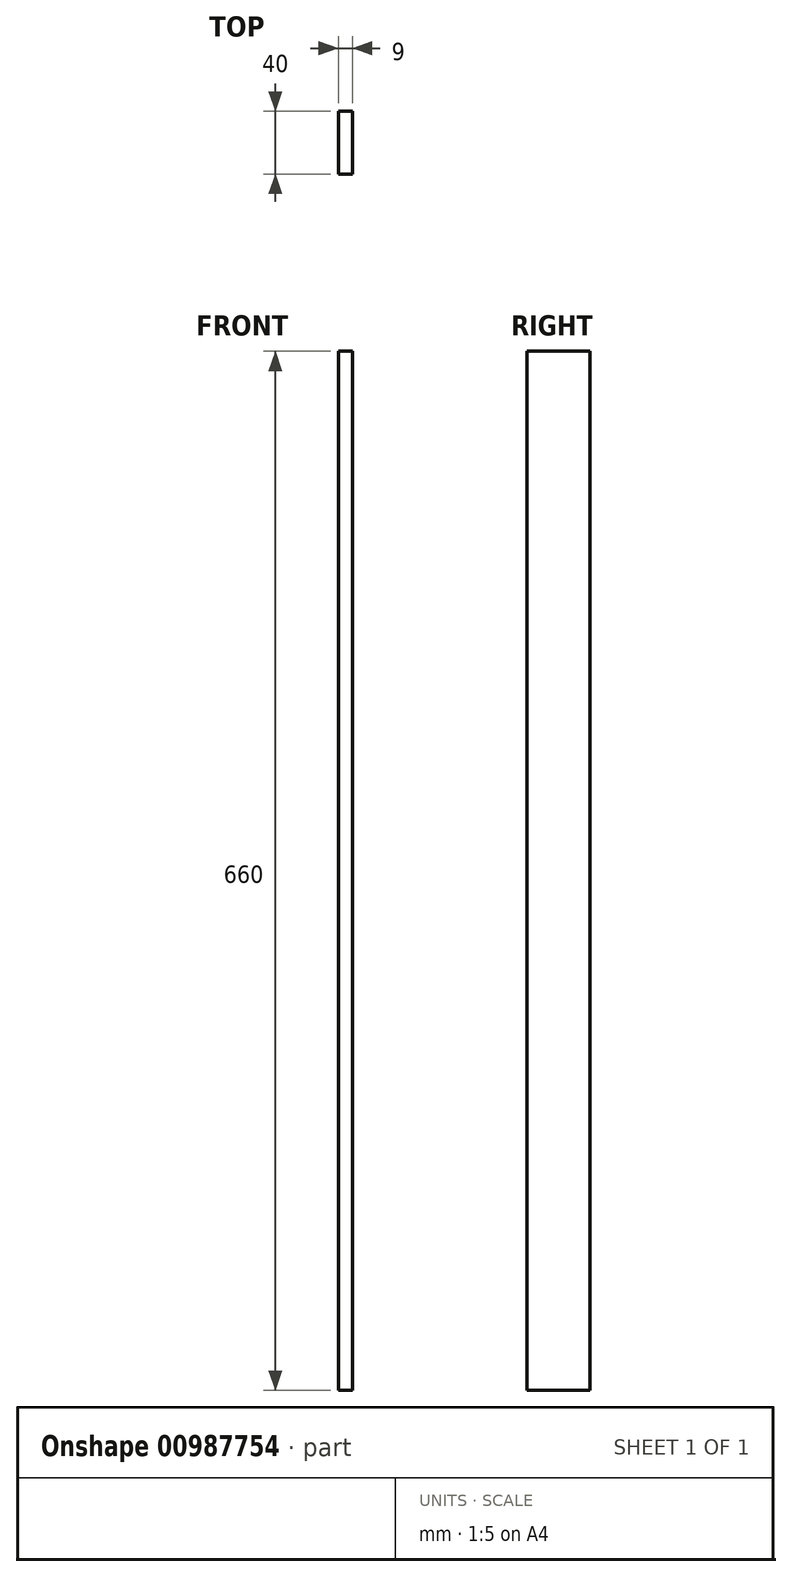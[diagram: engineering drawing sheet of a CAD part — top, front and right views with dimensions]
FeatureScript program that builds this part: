
annotation { "Feature Type Name" : "Feature", "Feature Type Description" : "" }
export const myFeature = defineFeature(function(context is Context, id is Id, definition is map)
    precondition{}
    {
        {
            var Q0;
            Q0=qCreatedBy(makeId("Top.planeOp"),FACE);
            var sketch = newSketch(context, id + "F0", { "sketchPlane" : qUnion([Q0])});
            skLineSegment(sketch, "E0.bottom", {"start": v(-4.5, -20) * mm, "end": v(4.5, -20) * mm});
            skLineSegment(sketch, "E0.top", {"start": v(-4.5, 20) * mm, "end": v(4.5, 20) * mm});
            skLineSegment(sketch, "E0.left", {"start": v(-4.5, -20) * mm, "end": v(-4.5, 20) * mm});
            skLineSegment(sketch, "E0.right", {"start": v(4.5, -20) * mm, "end": v(4.5, 20) * mm});
            skPoint(sketch, "E0.middle", {"position": v(0, 0) * mm});
            skSolve(sketch);
        }
        {
            var Q0;
            Q0 = qSketchRegion(id + "F0", true);
            extrude(context, id + "F1", {"entities" : qUnion([Q0]), "endBound" : BoundingType.SYMMETRIC, "oppositeDirection" : true, "depth" : 660 * mm, "offsetDistance" : 25 * mm});
        }
    });
